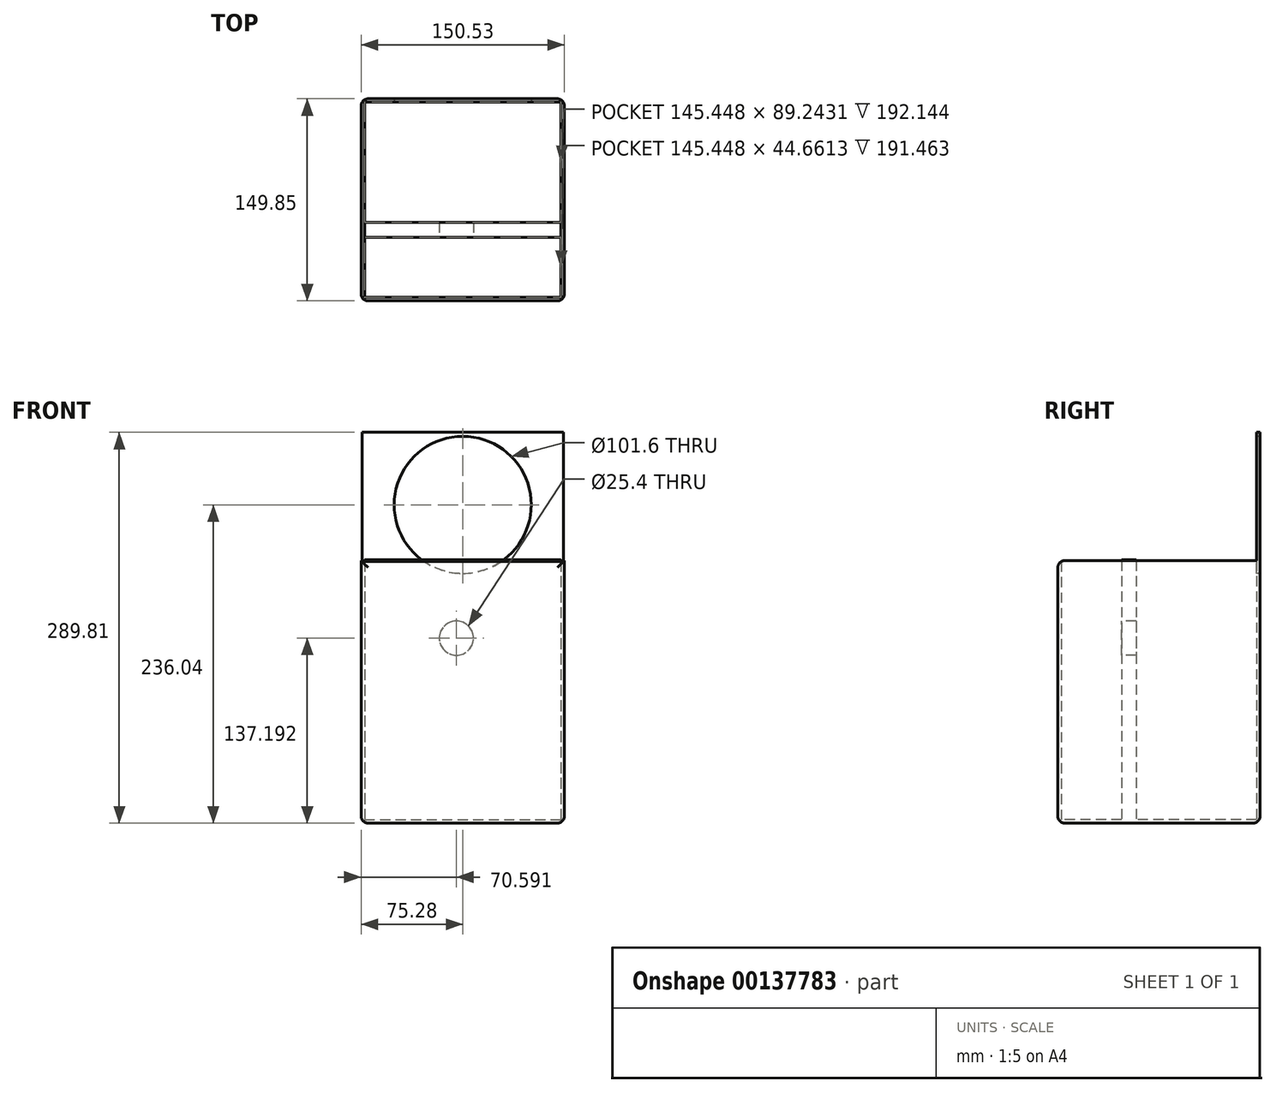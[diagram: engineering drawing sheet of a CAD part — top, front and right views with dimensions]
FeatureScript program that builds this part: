
annotation { "Feature Type Name" : "Feature", "Feature Type Description" : "" }
export const myFeature = defineFeature(function(context is Context, id is Id, definition is map)
    precondition{}
    {
        {
            var Q0;
            Q0=qCreatedBy(makeId("Top.planeOp"),FACE);
            var sketch = newSketch(context, id + "F0", { "sketchPlane" : qUnion([Q0])});
            skLineSegment(sketch, "E0.bottom", {"start": v(-75.28, 75.37) * mm, "end": v(75.25, 75.37) * mm});
            skLineSegment(sketch, "E0.top", {"start": v(-75.28, -74.48) * mm, "end": v(75.25, -74.48) * mm});
            skLineSegment(sketch, "E0.left", {"start": v(-75.28, 75.37) * mm, "end": v(-75.28, -74.48) * mm});
            skLineSegment(sketch, "E0.right", {"start": v(75.25, 75.37) * mm, "end": v(75.25, -74.48) * mm});
            skSolve(sketch);
        }
        {
            var Q0;
            Q0=makeQuery(id+"F0.imprint","IMPRINT",FACE,{"disambiguationData":[TD([[makeQuery(id+"F0.imprint","IMPRINT",EDGE,{"derivedFrom":sQuery(id+"F0.wireOp",EDGE,"E0.bottom")}),-1.0]])]});
            extrude(context, id + "F1", {"entities" : qUnion([Q0]), "depth" : 194.68 * mm});
        }
        {
            var Q0;
            Q0=makeQuery(id+"F1.opExtrude","CAP_FACE",FACE,{"disambiguationData":[OSD([sQuery(id+"F0.wireOp",EDGE,"E0.bottom"),sQuery(id+"F0.wireOp",EDGE,"E0.top"),sQuery(id+"F0.wireOp",EDGE,"E0.left"),sQuery(id+"F0.wireOp",EDGE,"E0.right")])],"isStart":false});
            shell(context, id + "F2", {"entities" : qUnion([Q0]), "thickness" : 2.54 * mm});
        }
        {
            var Q0;
            Q0=makeQuery(id+"F1.opExtrude","CAP_FACE",FACE,{"disambiguationData":[OSD([sQuery(id+"F0.wireOp",EDGE,"E0.bottom"),sQuery(id+"F0.wireOp",EDGE,"E0.top"),sQuery(id+"F0.wireOp",EDGE,"E0.left"),sQuery(id+"F0.wireOp",EDGE,"E0.right")])],"isStart":false});
            var sketch = newSketch(context, id + "F3", { "sketchPlane" : qUnion([Q0])});
            skLineSegment(sketch, "E1.bottom", {"start": v(-75.28, 75.37) * mm, "end": v(72.7, 75.37) * mm});
            skLineSegment(sketch, "E1.top", {"start": v(-75.28, 72.83) * mm, "end": v(72.7, 72.83) * mm});
            skLineSegment(sketch, "E1.left", {"start": v(-75.28, 75.37) * mm, "end": v(-75.28, 72.83) * mm});
            skLineSegment(sketch, "E1.right", {"start": v(72.7, 75.37) * mm, "end": v(72.7, 72.83) * mm});
            skLineSegment(sketch, "E2.bottom", {"start": v(75.25, 72.83) * mm, "end": v(72.7, 72.83) * mm});
            skLineSegment(sketch, "E2.top", {"start": v(75.25, 75.37) * mm, "end": v(72.7, 75.37) * mm});
            skLineSegment(sketch, "E2.left", {"start": v(75.25, 72.83) * mm, "end": v(75.25, 75.37) * mm});
            skLineSegment(sketch, "E2.right", {"start": v(72.7, 72.83) * mm, "end": v(72.7, 75.37) * mm});
            skSolve(sketch);
        }
        {
            var Q0;
            Q0=makeQuery(id+"F3.imprint","IMPRINT",FACE,{"disambiguationData":[TD([[makeQuery(id+"F3.imprint","IMPRINT",EDGE,{"derivedFrom":sQuery(id+"F3.wireOp",EDGE,"E1.bottom")}),-1.0]])]});
            var Q1;
            Q1=makeQuery(id+"F3.imprint","IMPRINT",FACE,{"disambiguationData":[TD([[makeQuery(id+"F3.imprint","IMPRINT",EDGE,{"derivedFrom":sQuery(id+"F3.wireOp",EDGE,"E2.bottom")}),-1.0]])]});
            extrude(context, id + "F4", {"entities" : qUnion([Q0, Q1]), "operationType" : NewBodyOperationType.ADD, "depth" : 95.13 * mm});
        }
        {
            var Q0;
            Q0=makeQuery(id+"F4.boolean.opBoolean","MERGE",FACE,{"derivedFrom":[makeQuery(id+"F2.opShell","OFFSET_FACE",FACE,{"disambiguationData":[OSD([sQuery(id+"F0.wireOp",EDGE,"E0.bottom")])]}),makeQuery(id+"F4.opExtrude","SWEPT_FACE",FACE,{"disambiguationData":[OSD([sQuery(id+"F3.wireOp",EDGE,"E1.top"),sQuery(id+"F3.wireOp",EDGE,"E2.bottom")])]})]});
            var sketch = newSketch(context, id + "F5", { "sketchPlane" : qUnion([Q0])});
            skLineSegment(sketch, "E3.bottom", {"start": v(39.71, 278.56) * mm, "end": v(-39.71, 278.56) * mm});
            skLineSegment(sketch, "E3.top", {"start": v(39.71, 193.52) * mm, "end": v(-39.71, 193.52) * mm});
            skLineSegment(sketch, "E3.left", {"start": v(39.71, 278.56) * mm, "end": v(39.71, 193.52) * mm});
            skLineSegment(sketch, "E3.right", {"start": v(-39.71, 278.56) * mm, "end": v(-39.71, 193.52) * mm});
            skPoint(sketch, "E3.middle", {"position": v(0, 236.04) * mm});
            skSolve(sketch);
        }
        {
            var Q0;
            Q0=sQuery(id+"F5.wireOp",VERTEX,"E3.middle");
            var Q1;
            Q1=makeQuery(id+"F1.opExtrude","SWEPT_BODY",BODY,{"disambiguationData":[OSD([sQuery(id+"F0.wireOp",EDGE,"E0.bottom"),sQuery(id+"F0.wireOp",EDGE,"E0.top"),sQuery(id+"F0.wireOp",EDGE,"E0.left"),sQuery(id+"F0.wireOp",EDGE,"E0.right")])]});
            hole(context, id + "F6", {"style" : HoleStyle.SIMPLE, "endStyle" : HoleEndStyle.THROUGH, "holeDiameter" : 101.6 * mm, "locations" : qUnion([Q0]), "scope" : qUnion([Q1]), "isTappedThrough" : true});
        }
        {
            var Q0;
            Q0=makeQuery(id+"F1.opExtrude","SWEPT_EDGE",EDGE,{"disambiguationData":[OSD([sQuery(id+"F0.wireOp",EDGE,"E0.top"),sQuery(id+"F0.wireOp",EDGE,"E0.left")])]});
            var Q1;
            Q1=makeQuery(id+"F4.boolean.opBoolean","MERGE",EDGE,{"derivedFrom":[makeQuery(id+"F1.opExtrude","SWEPT_EDGE",EDGE,{"disambiguationData":[OSD([sQuery(id+"F0.wireOp",EDGE,"E0.bottom"),sQuery(id+"F0.wireOp",EDGE,"E0.left")])]}),makeQuery(id+"F4.opExtrude","SWEPT_EDGE",EDGE,{"disambiguationData":[OSD([sQuery(id+"F3.wireOp",EDGE,"E1.bottom"),sQuery(id+"F3.wireOp",EDGE,"E1.left")])]})]});
            var Q2;
            Q2=makeQuery(id+"F4.boolean.opBoolean","MERGE",EDGE,{"derivedFrom":[makeQuery(id+"F1.opExtrude","SWEPT_EDGE",EDGE,{"disambiguationData":[OSD([sQuery(id+"F0.wireOp",EDGE,"E0.bottom"),sQuery(id+"F0.wireOp",EDGE,"E0.right")])]}),makeQuery(id+"F4.opExtrude","SWEPT_EDGE",EDGE,{"disambiguationData":[OSD([sQuery(id+"F3.wireOp",EDGE,"E2.top"),sQuery(id+"F3.wireOp",EDGE,"E2.left")])]})]});
            var Q3;
            Q3=makeQuery(id+"F1.opExtrude","SWEPT_EDGE",EDGE,{"disambiguationData":[OSD([sQuery(id+"F0.wireOp",EDGE,"E0.top"),sQuery(id+"F0.wireOp",EDGE,"E0.right")])]});
            var Q4;
            Q4=makeQuery(id+"F1.opExtrude","CAP_FACE",FACE,{"disambiguationData":[OSD([sQuery(id+"F0.wireOp",EDGE,"E0.bottom"),sQuery(id+"F0.wireOp",EDGE,"E0.top"),sQuery(id+"F0.wireOp",EDGE,"E0.left"),sQuery(id+"F0.wireOp",EDGE,"E0.right")])],"isStart":true});
            var Q5;
            Q5=makeQuery(id+"F1.opExtrude","CAP_EDGE",EDGE,{"disambiguationData":[OSD([sQuery(id+"F0.wireOp",EDGE,"E0.top")])],"isStart":false});
            fillet(context, id + "F7", {"entities" : qUnion([Q0, Q1, Q2, Q3, Q4, Q5]), "radius" : 5.08 * mm, "tangentPropagation" : true, "allowEdgeOverflow" : false});
        }
        {
            var Q0;
            Q0=makeQuery(id+"F2.opShell","OFFSET_FACE",FACE,{"disambiguationData":[OSD([sQuery(id+"F0.wireOp",EDGE,"E0.bottom"),sQuery(id+"F0.wireOp",EDGE,"E0.top"),sQuery(id+"F0.wireOp",EDGE,"E0.left"),sQuery(id+"F0.wireOp",EDGE,"E0.right")])]});
            var sketch = newSketch(context, id + "F8", { "sketchPlane" : qUnion([Q0])});
            skLineSegment(sketch, "E4.bottom", {"start": v(-72.74, -27.28) * mm, "end": v(72.7, -27.28) * mm});
            skLineSegment(sketch, "E4.top", {"start": v(-72.74, -16.41) * mm, "end": v(72.7, -16.41) * mm});
            skLineSegment(sketch, "E4.left", {"start": v(-72.74, -27.28) * mm, "end": v(-72.74, -16.41) * mm});
            skLineSegment(sketch, "E4.right", {"start": v(72.7, -27.28) * mm, "end": v(72.7, -16.41) * mm});
            skSolve(sketch);
        }
        {
            var Q0;
            Q0=makeQuery(id+"F8.imprint","IMPRINT",FACE,{"disambiguationData":[TD([[makeQuery(id+"F8.imprint","IMPRINT",EDGE,{"derivedFrom":sQuery(id+"F8.wireOp",EDGE,"E4.bottom")}),1.0]])]});
            extrude(context, id + "F9", {"entities" : qUnion([Q0]), "operationType" : NewBodyOperationType.ADD, "depth" : 192.73 * mm});
        }
        {
            var Q0;
            Q0=makeQuery(id+"F9.opExtrude","SWEPT_FACE",FACE,{"disambiguationData":[OSD([sQuery(id+"F8.wireOp",EDGE,"E4.bottom")])]});
            var sketch = newSketch(context, id + "F10", { "sketchPlane" : qUnion([Q0])});
            skCircle(sketch, "E5", {"center": v(-4.69, 137.2) * mm, "radius": 28.29 * mm});
            skSolve(sketch);
        }
        {
            var Q0;
            Q0=sQuery(id+"F10.wireOp",VERTEX,"E5.center");
            var Q1;
            Q1=makeQuery(id+"F1.opExtrude","SWEPT_BODY",BODY,{"disambiguationData":[OSD([sQuery(id+"F0.wireOp",EDGE,"E0.bottom"),sQuery(id+"F0.wireOp",EDGE,"E0.top"),sQuery(id+"F0.wireOp",EDGE,"E0.left"),sQuery(id+"F0.wireOp",EDGE,"E0.right")])]});
            hole(context, id + "F11", {"style" : HoleStyle.SIMPLE, "endStyle" : HoleEndStyle.BLIND, "holeDiameter" : 25.4 * mm, "holeDepth" : 12.7 * mm, "locations" : qUnion([Q0]), "scope" : qUnion([Q1])});
        }
    });
